# Revit family: TC-Series-WS38-WS54
name_source: partatom
category: Mechanical Equipment
units: mm (PartAtom-declared; Revit-internal decimal feet)

## family parameters
Cut with Voids When Loaded = Yes
Host = Face
Part Type = Normal
Room Calculation Point = No
Round Connector Dimension = Use Diameter
Shared = Yes

## types (2) — shared parameters
Default Elevation = 4' - 0"
EFFICIENCY RATING = 0.00%
FRAME MATERIAL = <By Category>
HVAC BTU OUTPUT = 0 Btu/h
UNIT HEIGHT = 2' - 5 3/4"
UNIT WEIGHT = 0.00 kgf
flue connection size = 0' - 6"

## per-type parameters (varying)
| type | FACE HEIGHT | FACE WIDTH | FRAME HEIGHT | FRAME WIDTH | FUEL CNSUMPTION | STAND OFF HEIGHT | UNIT WIDTH |
| TCWS 38D2 | 1' - 4 3/16" | 3' - 4 7/16" | 3' - 9 1/8" | 5' - 1 5/8" |  | 0' - 2" | 4' - 0 7/16" |
| TCWS 54D2 | 1' - 6 3/16" | 4' - 6 7/16" | 4' - 7 1/16" | 6' - 2 3/4" | AS SPECIFIED | 0' - 6" | 5' - 2 7/16" |

## geometry (parser evidence)
native form markers: Sweep x4
no freeform markers — native parametric forms only
